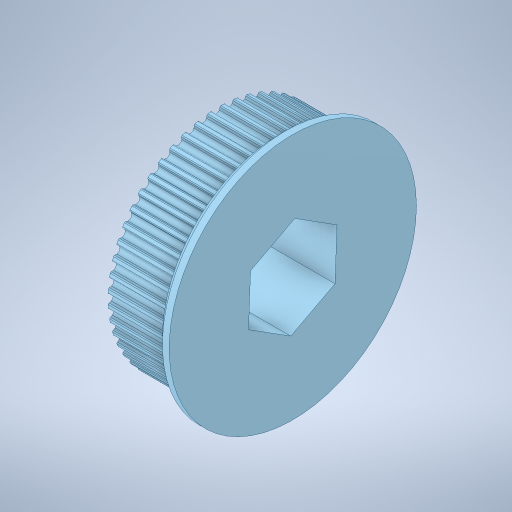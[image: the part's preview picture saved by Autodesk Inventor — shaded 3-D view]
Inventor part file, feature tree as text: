
AUTODESK INVENTOR PART (.ipt)
format: ipt  version: 2023.3 (Build 273359000, 359)  size: 603,648 bytes
history: native  units: in
note: dims shown in document units (in); Inventor stores cm internally (conversion verified against a paired STEP export)
features: extrude x1, sketch x1, other x1
ambient origin geometry x8: Origin, YZ Plane, XZ Plane, XY Plane, X Axis, Y Axis, Z Axis, Center Point
bodies: Solid1 (feature_tree)
feature tree (3):
  extrude  "Extrusion1"  Depth=0.2in
  sketch  "Sketch1"  dims[d0=0.875in d1=0.2283in d2=1.5748in d4=360.0deg d6=0.2in d7=0.0in]
  other  "Part 1"
